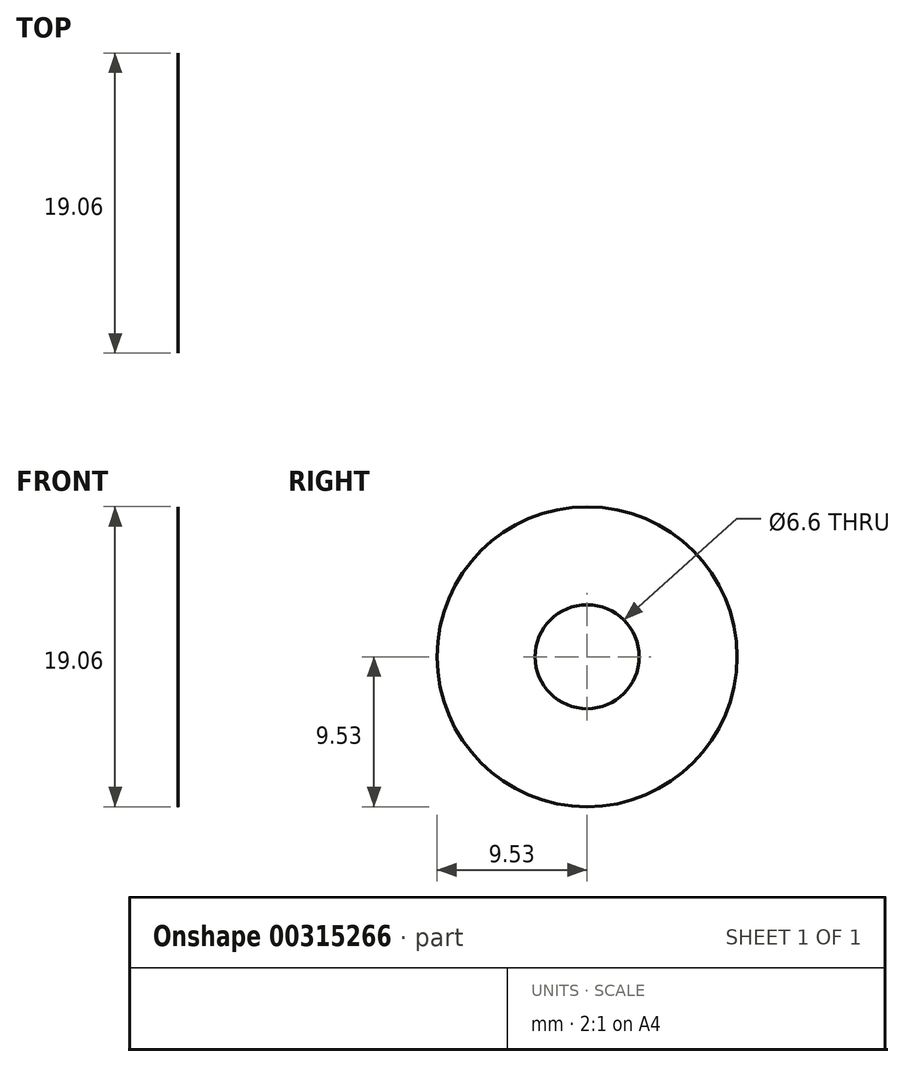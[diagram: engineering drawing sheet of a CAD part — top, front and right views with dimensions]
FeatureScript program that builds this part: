
annotation { "Feature Type Name" : "Feature", "Feature Type Description" : "" }
export const myFeature = defineFeature(function(context is Context, id is Id, definition is map)
    precondition{}
    {
        {
            var Q0;
            Q0=qCreatedBy(makeId("Right.planeOp"),FACE);
            var sketch = newSketch(context, id + "F0", { "sketchPlane" : qUnion([Q0])});
            skCircle(sketch, "E0", {"center": v(0, 0) * mm, "radius": 9.53 * mm});
            skCircle(sketch, "E1", {"center": v(0, 0) * mm, "radius": 3.3 * mm});
            skSolve(sketch);
        }
        {
            var Q0;
            Q0 = qSketchRegion(id + "F0", true);
            extrude(context, id + "F1", {"entities" : qUnion([Q0]), "depth" : 1 / 406.4 * mm});
        }
    });
